# Revit family: Sanitary_Showers_hansgrohe_26864USA-Rainfinity-Hand-shower-130-3jet_NEW
name_source: partatom
category: Plumbing Fixtures
revit_build: Autodesk Revit 2018 (Build: 20170223_1515(x64)
units: mm (PartAtom-declared; Revit-internal decimal feet)

## family parameters
Always vertical = No
Cut with Voids When Loaded = No
OmniClass Number = 23.31.17.00
OmniClass Title = Showers
Part Type = Normal
Room Calculation Point = No
Round Connector Dimension = Use Diameter
Shared = No
Work Plane-Based = Yes

## types (4) — shared parameters
Always visible = Yes
BIMobject category = Showers
Connector Description = Water Inlet 1/2
Default Elevation = 4' - 0"
Description = Rainfinity Hand shower 130 3jet 2.5 GPM
Diameter = 1"
Edition number = 1
IFC Classification = Sanitary Terminal
Manufacturer = Hansgrohe
Manufacturer name = hansgrohe
Material 1 = Hansgrohe - Plastic - Graphite
Model = 26864USA
OmniClass Code = 23-31 17 00
OmniClass Description = Showers
Product Guid = 91d033cd-eee4-4c88-a11a-a7ccc79b5154
Product SKU = 26864USA
Product data url = https://bimobject.com
Product family = Rainfinity
Product group = Hand showers
Product name = 26864USA Rainfinity Hand shower 130 3jet 2.5 GPM
Product url = https://www.hansgrohe.com
QR code = https://bimobject.com
URL = https://www.hansgrohe.com
Weight Net (Kg) = 465

## per-type parameters (varying)
| type | Material 2 |
| 821 Brushed Nickel | Hansgrohe - Metal - 821 Brushed Nickel |
| 701 Matt White | Hansgrohe - Metal - 701 Matt White |
| 671 Matt Black | Hansgrohe - Metal - 671 Matt Black |
| 001 Chrome | Hansgrohe - Metal - 001 Chrome |

## geometry (parser evidence)
native form markers: Sweep x4
no freeform markers — native parametric forms only
